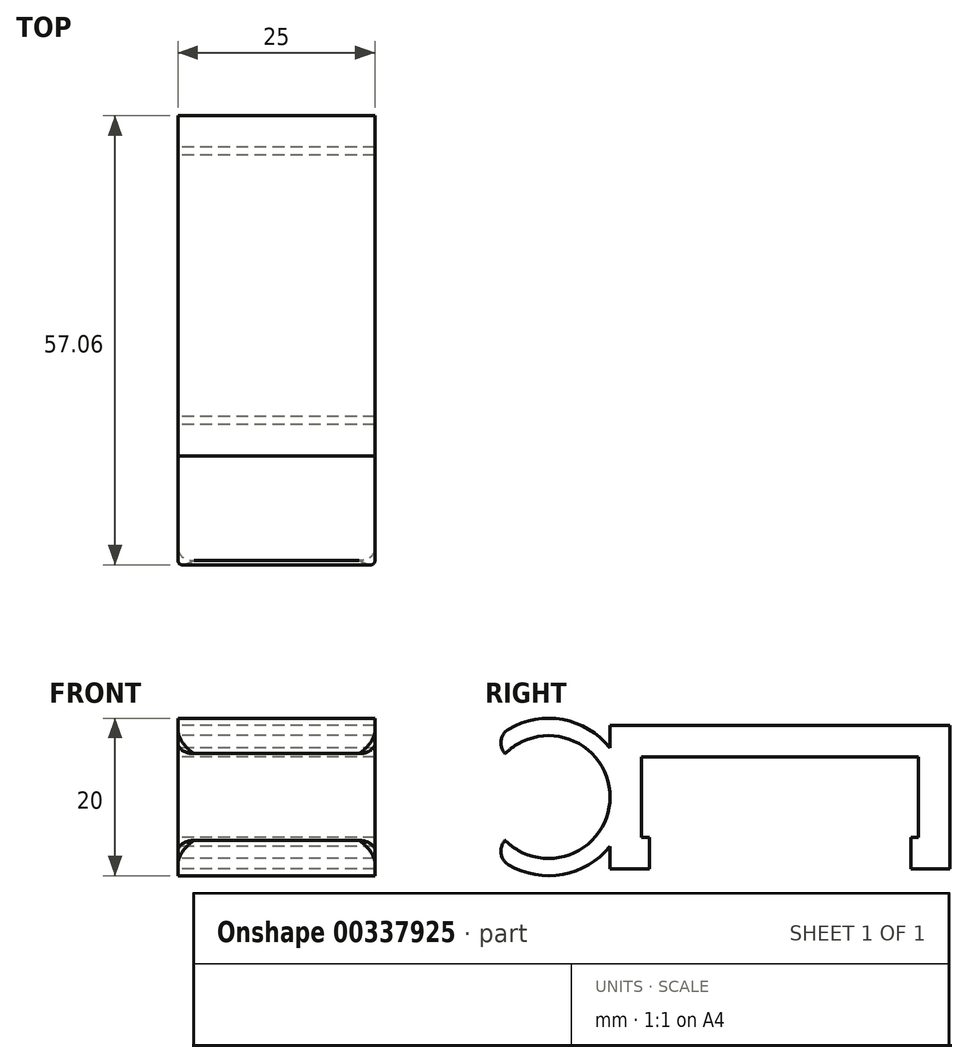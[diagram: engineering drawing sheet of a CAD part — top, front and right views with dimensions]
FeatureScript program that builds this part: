
annotation { "Feature Type Name" : "Feature", "Feature Type Description" : "" }
export const myFeature = defineFeature(function(context is Context, id is Id, definition is map)
    precondition{}
    {
        {
            var Q0;
            Q0=qCreatedBy(makeId("Right.planeOp"),FACE);
            var sketch = newSketch(context, id + "F0", { "sketchPlane" : qUnion([Q0])});
            skLineSegment(sketch, "E0", {"start": v(0, 0) * mm, "end": v(17.5, 0) * mm});
            skLineSegment(sketch, "E1", {"start": v(17.5, 0) * mm, "end": v(17.5, -10.05) * mm});
            skLineSegment(sketch, "E2", {"start": v(17.5, -10.05) * mm, "end": v(14.2, -10.05) * mm});
            skLineSegment(sketch, "E3", {"start": v(14.2, -10.05) * mm, "end": v(14.2, -6.25) * mm});
            skLineSegment(sketch, "E4", {"start": v(14.2, -6.25) * mm, "end": v(8.2, -6.25) * mm});
            skLineSegment(sketch, "E5", {"start": v(8.2, -6.25) * mm, "end": v(8.2, -27.41) * mm});
            skLineSegment(sketch, "E6", {"start": v(8.2, -27.41) * mm, "end": v(-8.2, -27.41) * mm});
            skLineSegment(sketch, "E7", {"start": v(-8.2, -27.41) * mm, "end": v(-8.2, -6.25) * mm});
            skLineSegment(sketch, "E8", {"start": v(-8.2, -6.25) * mm, "end": v(-14.2, -6.25) * mm});
            skLineSegment(sketch, "E9", {"start": v(-14.2, -6.25) * mm, "end": v(-14.2, -10.05) * mm});
            skLineSegment(sketch, "E10", {"start": v(-14.2, -10.05) * mm, "end": v(-17.5, -10.05) * mm});
            skLineSegment(sketch, "E11", {"start": v(-17.5, -10.05) * mm, "end": v(-17.5, 0) * mm});
            skLineSegment(sketch, "E12", {"start": v(-17.5, 0) * mm, "end": v(0, 0) * mm});
            skLineSegment(sketch, "E13.0", {"start": v(17.6, -10.15) * mm, "end": v(16.6, -10.15) * mm});
            skLineSegment(sketch, "E13.1", {"start": v(17.6, 0.1) * mm, "end": v(17.6, -10.15) * mm});
            skLineSegment(sketch, "E13.2", {"start": v(-16.6, -10.15) * mm, "end": v(-17.6, -10.15) * mm});
            skLineSegment(sketch, "E13.3", {"start": v(-17.6, -10.15) * mm, "end": v(-17.6, 0.1) * mm});
            skLineSegment(sketch, "E13.4", {"start": v(-17.6, 0.1) * mm, "end": v(0, 0.1) * mm});
            skLineSegment(sketch, "E13.5", {"start": v(0, 0.1) * mm, "end": v(17.6, 0.1) * mm});
            skLineSegment(sketch, "E14.0", {"start": v(21.6, -14.15) * mm, "end": v(16.6, -14.15) * mm});
            skLineSegment(sketch, "E14.1", {"start": v(21.6, 4.1) * mm, "end": v(21.6, -14.15) * mm});
            skLineSegment(sketch, "E14.2", {"start": v(-16.6, -14.15) * mm, "end": v(-21.6, -14.15) * mm});
            skLineSegment(sketch, "E14.3", {"start": v(-21.6, -14.15) * mm, "end": v(-21.6, 4.1) * mm});
            skLineSegment(sketch, "E14.4", {"start": v(-21.6, 4.1) * mm, "end": v(0, 4.1) * mm});
            skLineSegment(sketch, "E14.5", {"start": v(0, 4.1) * mm, "end": v(21.6, 4.1) * mm});
            skLineSegment(sketch, "E15", {"start": v(-16.6, -10.15) * mm, "end": v(-16.6, -14.15) * mm});
            skLineSegment(sketch, "E16", {"start": v(16.6, -10.15) * mm, "end": v(16.6, -14.15) * mm});
            skLineSegment(sketch, "E17", {"start": v(-21.6, -5.03) * mm, "end": v(-29.4, -5.03) * mm, "construction": true});
            skCircle(sketch, "E18", {"center": v(-29.4, -5.03) * mm, "radius": 7.8 * mm});
            skCircle(sketch, "E19", {"center": v(-29.4, -5.03) * mm, "radius": 10 * mm});
            skLineSegment(sketch, "E20", {"start": v(-21.6, -5.03) * mm, "end": v(-39.4, -5.03) * mm, "construction": true});
            skLineSegment(sketch, "E21", {"start": v(-29.4, -5.03) * mm, "end": v(-36.47, 2.05) * mm});
            skLineSegment(sketch, "E22", {"start": v(-29.4, -5.03) * mm, "end": v(-36.47, -12.1) * mm});
            skSolve(sketch);
        }
        {
            var Q0;
            Q0=makeQuery(id+"F0.imprint","IMPRINT",FACE,{"disambiguationData":[TD([[makeQuery(id+"F0.imprint","IMPRINT",EDGE,{"derivedFrom":sQuery(id+"F0.wireOp",EDGE,"E13.0")}),1.0]])]});
            extrude(context, id + "F1", {"entities" : qUnion([Q0]), "depth" : 25 * mm});
        }
        {
            var Q0;
            {var subQ0=sQuery(id+"F0.wireOp",EDGE,"E19");var subQ1=sQuery(id+"F0.wireOp",EDGE,"E14.3");var subQ2=makeQuery(id+"F0.imprint","INTERSECT",VERTEX,{"disambiguationData":[OD(1.0)],"derivedFrom":[subQ1,subQ0]});Q0=makeQuery(id+"F0.imprint","IMPRINT",FACE,{"disambiguationData":[TD([[makeQuery(id+"F0.imprint","IMPRINT",EDGE,{"disambiguationData":[TD([[subQ2,1.0]])],"derivedFrom":subQ1}),1.0]])]});}
            var Q1;
            {var subQ0=sQuery(id+"F0.wireOp",EDGE,"E19");var subQ1=sQuery(id+"F0.wireOp",EDGE,"E14.3");var subQ2=makeQuery(id+"F0.imprint","INTERSECT",VERTEX,{"disambiguationData":[OD(0.0)],"derivedFrom":[subQ1,subQ0]});Q1=makeQuery(id+"F0.imprint","IMPRINT",FACE,{"disambiguationData":[TD([[makeQuery(id+"F0.imprint","IMPRINT",EDGE,{"disambiguationData":[TD([[subQ2,-1.0]])],"derivedFrom":subQ1}),1.0]])]});}
            var Q2;
            {var subQ0=sQuery(id+"F0.wireOp",EDGE,"E19");var subQ1=sQuery(id+"F0.wireOp",EDGE,"E14.3");var subQ2=makeQuery(id+"F0.imprint","INTERSECT",VERTEX,{"disambiguationData":[OD(0.0)],"derivedFrom":[subQ1,subQ0]});Q2=makeQuery(id+"F0.imprint","IMPRINT",FACE,{"disambiguationData":[TD([[makeQuery(id+"F0.imprint","IMPRINT",EDGE,{"disambiguationData":[TD([[subQ2,-1.0]])],"derivedFrom":subQ1}),-1.0]])]});}
            extrude(context, id + "F2", {"entities" : qUnion([Q0, Q1, Q2]), "operationType" : NewBodyOperationType.ADD, "depth" : 25 * mm});
        }
        {
            var Q0;
            Q0=makeQuery(id+"F2.opExtrude","CAP_EDGE",EDGE,{"disambiguationData":[OSD([sQuery(id+"F0.wireOp",EDGE,"E22")])],"isStart":false});
            var Q1;
            Q1=makeQuery(id+"F2.opExtrude","CAP_EDGE",EDGE,{"disambiguationData":[OSD([sQuery(id+"F0.wireOp",EDGE,"E21")])],"isStart":false});
            var Q2;
            Q2=makeQuery(id+"F2.opExtrude","CAP_EDGE",EDGE,{"disambiguationData":[OSD([sQuery(id+"F0.wireOp",EDGE,"E22")])],"isStart":true});
            var Q3;
            Q3=makeQuery(id+"F2.opExtrude","CAP_EDGE",EDGE,{"disambiguationData":[OSD([sQuery(id+"F0.wireOp",EDGE,"E21")])],"isStart":true});
            fillet(context, id + "F3", {"entities" : qUnion([Q0, Q1, Q2, Q3]), "radius" : 2 * mm, "tangentPropagation" : true, "allowEdgeOverflow" : false});
        }
        {
            var Q0;
            Q0=makeQuery(id+"F2.opExtrude","SWEPT_EDGE",EDGE,{"disambiguationData":[OSD([sQuery(id+"F0.wireOp",EDGE,"E19"),sQuery(id+"F0.wireOp",EDGE,"E21")])]});
            var Q1;
            Q1=makeQuery(id+"F2.opExtrude","SWEPT_EDGE",EDGE,{"disambiguationData":[OSD([sQuery(id+"F0.wireOp",EDGE,"E19"),sQuery(id+"F0.wireOp",EDGE,"E22")])]});
            fillet(context, id + "F4", {"entities" : qUnion([Q0, Q1]), "radius" : 2 * mm, "allowEdgeOverflow" : false});
        }
    });
